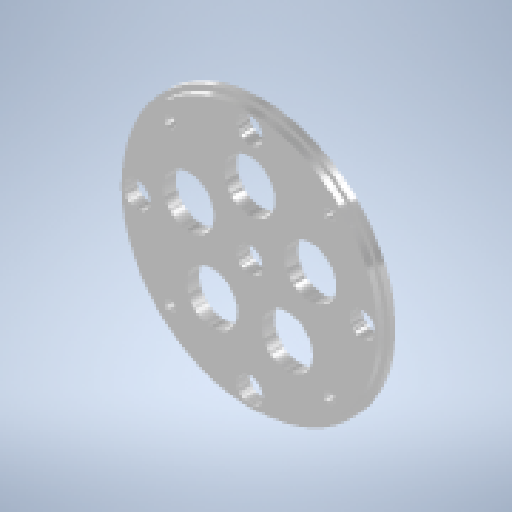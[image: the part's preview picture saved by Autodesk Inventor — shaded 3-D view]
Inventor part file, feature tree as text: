
AUTODESK INVENTOR PART (.ipt)
format: ipt  version: 2024 (Build 280153000, 153)  size: 196,096 bytes
history: native  units: mm
features: sketch x6, extrude x3, hole x3, pattern_circular x2, other x1
ambient origin geometry x8: Origin, YZ Plane, XZ Plane, XY Plane, X Axis, Y Axis, Z Axis, Center Point
bodies: Body1 (feature_tree)
feature tree (15):
  other  "ソリッド1"
  extrude  "押し出し1"  Depth=100.0mm
  extrude  "押し出し2"  Depth=2.5mm TaperAngle=0.0deg
  hole  "穴1"  [1 undecoded]
  hole  "穴2"  [1 undecoded]
  pattern_circular  "円形状パターン1"  [2 undecoded]
  hole  "穴3"  [1 undecoded]
  pattern_circular  "円形状パターン2"  Angle=45.0deg  [1 undecoded]
  extrude  "押し出し3"  Depth=40.0mm TaperAngle=360.0deg
  sketch  "スケッチ1"
  sketch  "スケッチ2"
  sketch  "スケッチ3"
  sketch  "スケッチ4"
  sketch  "スケッチ5"
  sketch  "スケッチ6"
note: 6 required parameter values undecoded (feature->parameter linkage not recoverable at this tier; creation-order binding heuristic only, values carry confidence <= 0.55)
